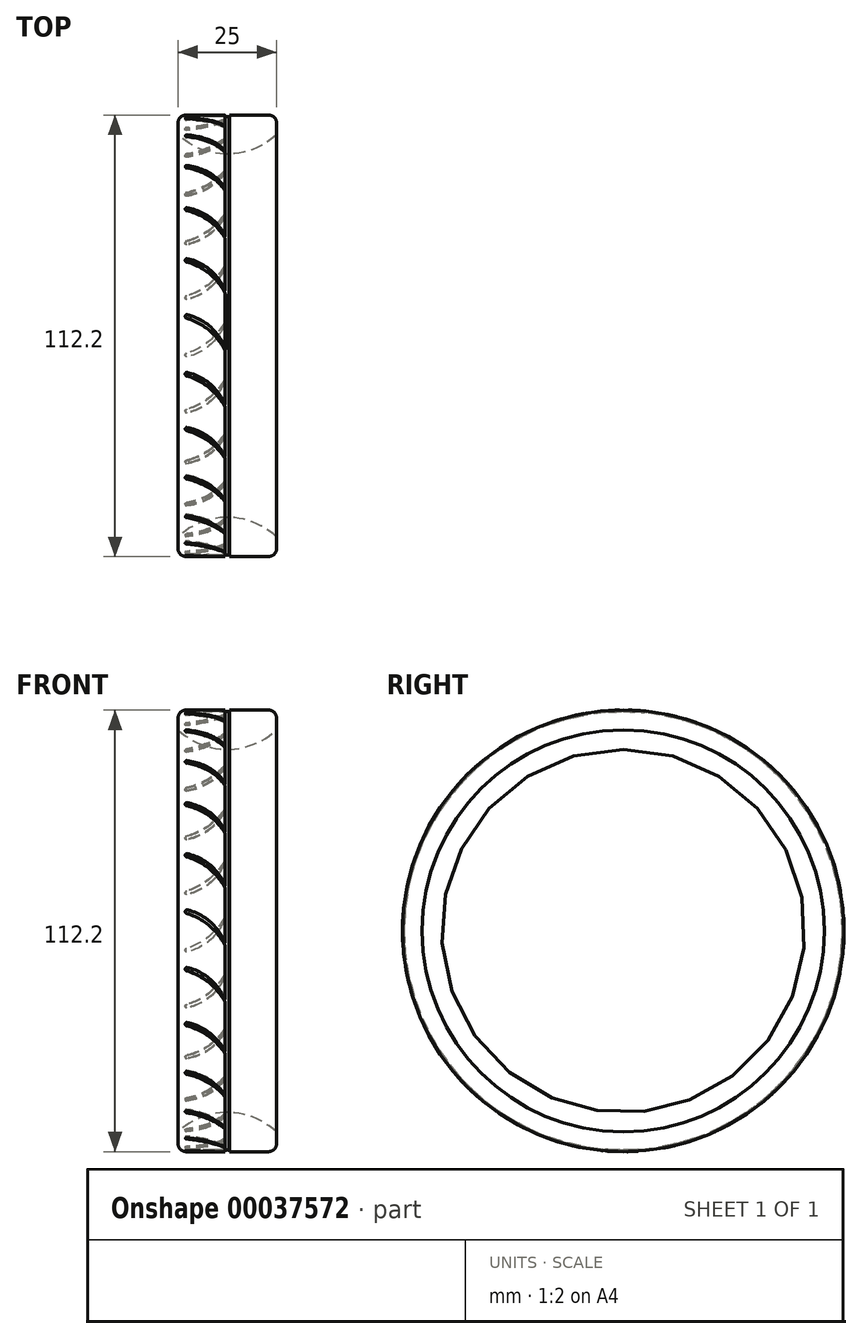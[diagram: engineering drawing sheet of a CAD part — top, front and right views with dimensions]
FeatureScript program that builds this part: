
annotation { "Feature Type Name" : "Feature", "Feature Type Description" : "" }
export const myFeature = defineFeature(function(context is Context, id is Id, definition is map)
    precondition{}
    {
        {
            var Q0;
            Q0=qCreatedBy(makeId("Top.planeOp"),FACE);
            var sketch = newSketch(context, id + "F0", { "sketchPlane" : qUnion([Q0])});
            skLineSegment(sketch, "E0", {"start": v(-134.1, 0) * mm, "end": v(143.87, 0) * mm, "construction": true});
            skLineSegment(sketch, "E1.left", {"start": v(-12.5, 54.1) * mm, "end": v(-12.5, 51.1) * mm});
            skLineSegment(sketch, "E1.right", {"start": v(12.5, 54.1) * mm, "end": v(12.5, 51.1) * mm});
            skArc(sketch, "E2", {"start": v(-12.5, 51.1) * mm, "mid": v(0, 46.14) * mm, "end": v(12.5, 51.1) * mm});
            skLineSegment(sketch, "E3", {"start": v(-10.5, 56.1) * mm, "end": v(-0.6, 56.1) * mm});
            skPoint(sketch, "E4.visualSharp", {"position": v(-12.5, 56.1) * mm});
            skArc(sketch, "E4.filletArc", {"start": v(-10.5, 56.1) * mm, "mid": v(-11.91, 55.51) * mm, "end": v(-12.5, 54.1) * mm});
            skPoint(sketch, "E5.visualSharp", {"position": v(12.5, 56.1) * mm});
            skArc(sketch, "E5.filletArc", {"start": v(12.5, 54.1) * mm, "mid": v(11.91, 55.51) * mm, "end": v(10.5, 56.1) * mm});
            skLineSegment(sketch, "E6.rect.bottom", {"start": v(0.6, 55.7) * mm, "end": v(-0.6, 55.7) * mm});
            skLineSegment(sketch, "E6.rect.left", {"start": v(0.6, 55.7) * mm, "end": v(0.6, 56.1) * mm});
            skLineSegment(sketch, "E6.rect.right", {"start": v(-0.6, 55.7) * mm, "end": v(-0.6, 56.1) * mm});
            skLineSegment(sketch, "E7.trimOffspring", {"start": v(0.6, 56.1) * mm, "end": v(10.5, 56.1) * mm});
            skSolve(sketch);
        }
        {
            var Q0;
            Q0=makeQuery(id+"F0.imprint","IMPRINT",FACE,{"disambiguationData":[TD([[makeQuery(id+"F0.imprint","IMPRINT",EDGE,{"derivedFrom":sQuery(id+"F0.wireOp",EDGE,"E1.left")}),1.0]])]});
            var Q1;
            Q1=sQuery(id+"F0.wireOp",EDGE,"E0");
            revolve(context, id + "F1", {"entities" : qUnion([Q0]), "axis" : qUnion([Q1]), "revolveType" : RevolveType.FULL});
        }
        {
            var Q0;
            Q0=qCreatedBy(makeId("Top.planeOp"),FACE);
            cPlane(context, id + "F2", {"entities" : qUnion([Q0]), "cplaneType" : CPlaneType.OFFSET, "offset" : 56.1 * mm, "width" : 150 * mm, "height" : 150 * mm});
        }
        {
            var Q0;
            Q0=qCreatedBy(makeId("Top.planeOp"),FACE);
            var sketch = newSketch(context, id + "F3", { "sketchPlane" : qUnion([Q0])});
            skLineSegment(sketch, "E8", {"start": v(-88.22, 0) * mm, "end": v(82.6, 0) * mm, "construction": true});
            skSolve(sketch);
        }
        {
            var Q0;
            Q0=qCreatedBy(id+"F2.planeOp",FACE);
            var sketch = newSketch(context, id + "F4", { "sketchPlane" : qUnion([Q0])});
            skArc(sketch, "E9", {"start": v(0, -5.08) * mm, "mid": v(-3.64, 1.64) * mm, "end": v(-10.3, 5.36) * mm});
            skArc(sketch, "E10", {"start": v(0, -5.08) * mm, "mid": v(-4.05, 0.87) * mm, "end": v(-10.3, 4.43) * mm});
            skArc(sketch, "E11", {"start": v(-10.3, 5.36) * mm, "mid": v(-10.68, 4.9) * mm, "end": v(-10.3, 4.43) * mm});
            skArc(sketch, "E12.MirrorCS", {"start": v(0, -5.08) * mm, "mid": v(3.64, 1.64) * mm, "end": v(10.3, 5.36) * mm});
            skArc(sketch, "E13.MirrorCS", {"start": v(0, -5.08) * mm, "mid": v(4.05, 0.87) * mm, "end": v(10.3, 4.43) * mm});
            skArc(sketch, "E14.MirrorCS", {"start": v(10.3, 5.36) * mm, "mid": v(10.68, 4.9) * mm, "end": v(10.3, 4.43) * mm});
            skSolve(sketch);
        }
        {
            var Q0;
            Q0=makeQuery(id+"F4.imprint","IMPRINT",FACE,{"disambiguationData":[TD([[makeQuery(id+"F4.imprint","IMPRINT",EDGE,{"derivedFrom":sQuery(id+"F4.wireOp",EDGE,"E9")}),1.0]])]});
            var Q1;
            Q1=makeQuery(id+"F4.imprint","IMPRINT",FACE,{"disambiguationData":[TD([[makeQuery(id+"F4.imprint","IMPRINT",EDGE,{"derivedFrom":sQuery(id+"F4.wireOp",EDGE,"E12.MirrorCS")}),-1.0]])]});
            var Q2;
            Q2=makeQuery(id+"F1.opRevolve","SWEPT_FACE",FACE,{"disambiguationData":[OSD([sQuery(id+"F0.wireOp",EDGE,"E6.rect.bottom")])]});
            extrude(context, id + "F5", {"entities" : qUnion([Q0, Q1]), "operationType" : NewBodyOperationType.REMOVE, "endBound" : BoundingType.UP_TO_SURFACE, "oppositeDirection" : true, "endBoundEntityFace" : qUnion([Q2]), "depth" : 1 * mm});
        }
        {
            var Q0;
            Q0=makeQuery(id+"F5.boolean.opBoolean","COPY",FACE,{"derivedFrom":makeQuery(id+"F5.opExtrude","SWEPT_FACE",FACE,{"disambiguationData":[OSD([sQuery(id+"F4.wireOp",EDGE,"E9")])]})});
            var Q1;
            Q1=makeQuery(id+"F5.boolean.opBoolean","COPY",FACE,{"derivedFrom":makeQuery(id+"F5.opExtrude","SWEPT_FACE",FACE,{"disambiguationData":[OSD([sQuery(id+"F4.wireOp",EDGE,"E11")])]})});
            var Q2;
            Q2=makeQuery(id+"F5.boolean.opBoolean","COPY",FACE,{"derivedFrom":makeQuery(id+"F5.opExtrude","SWEPT_FACE",FACE,{"disambiguationData":[OSD([sQuery(id+"F4.wireOp",EDGE,"E12.MirrorCS")])]})});
            var Q3;
            Q3=makeQuery(id+"F5.boolean.opBoolean","COPY",FACE,{"derivedFrom":makeQuery(id+"F5.opExtrude","SWEPT_FACE",FACE,{"disambiguationData":[OSD([sQuery(id+"F4.wireOp",EDGE,"E10")])]})});
            var Q4;
            Q4=makeQuery(id+"F5.boolean.opBoolean","COPY",FACE,{"derivedFrom":makeQuery(id+"F5.opExtrude","SWEPT_FACE",FACE,{"disambiguationData":[OSD([sQuery(id+"F4.wireOp",EDGE,"E13.MirrorCS")])]})});
            var Q5;
            Q5=makeQuery(id+"F5.boolean.opBoolean","COPY",FACE,{"derivedFrom":makeQuery(id+"F5.opExtrude","SWEPT_FACE",FACE,{"disambiguationData":[OSD([sQuery(id+"F4.wireOp",EDGE,"E14.MirrorCS")])]})});
            var Q6;
            Q6=sQuery(id+"F3.wireOp",EDGE,"E8");
            circularPattern(context, id + "F6", {"faces" : qUnion([Q0, Q1, Q2, Q3, Q4, Q5]), "axis" : qUnion([Q6]), "angle" : 360 * degree, "instanceCount" : 24, "equalSpace" : true, "patternType" : PatternType.FACE});
        }
        {
            var Q0;
            Q0=makeQuery(id+"F6.opPattern","SPLIT",EDGE,{"disambiguationData":[OD(0.0)],"derivedFrom":makeQuery(id+"F1.opRevolve","SWEPT_EDGE",EDGE,{"disambiguationData":[OSD([sQuery(id+"F0.wireOp",EDGE,"E6.rect.bottom"),sQuery(id+"F0.wireOp",EDGE,"E6.rect.left")])]})});
            var Q1;
            Q1=makeQuery(id+"F5.boolean.opBoolean","COPY",EDGE,{"derivedFrom":makeQuery(id+"F5.opExtrude","TWEAK_EDGE",EDGE,{"derivedFrom":[makeQuery(id+"F1.opRevolve","SWEPT_FACE",FACE,{"disambiguationData":[OSD([sQuery(id+"F0.wireOp",EDGE,"E6.rect.bottom")])]}),makeQuery(id+"F4.imprint","IMPRINT",EDGE,{"derivedFrom":sQuery(id+"F4.wireOp",EDGE,"E12.MirrorCS")})]})});
            var Q2;
            Q2=makeQuery(id+"F5.boolean.opBoolean","COPY",EDGE,{"derivedFrom":makeQuery(id+"F5.opExtrude","TWEAK_EDGE",EDGE,{"derivedFrom":[makeQuery(id+"F1.opRevolve","SWEPT_FACE",FACE,{"disambiguationData":[OSD([sQuery(id+"F0.wireOp",EDGE,"E6.rect.bottom")])]}),makeQuery(id+"F4.imprint","IMPRINT",EDGE,{"derivedFrom":sQuery(id+"F4.wireOp",EDGE,"E14.MirrorCS")})]})});
            var Q3;
            Q3=makeQuery(id+"F5.boolean.opBoolean","COPY",EDGE,{"derivedFrom":makeQuery(id+"F5.opExtrude","TWEAK_EDGE",EDGE,{"derivedFrom":[makeQuery(id+"F1.opRevolve","SWEPT_FACE",FACE,{"disambiguationData":[OSD([sQuery(id+"F0.wireOp",EDGE,"E6.rect.bottom")])]}),makeQuery(id+"F4.imprint","IMPRINT",EDGE,{"derivedFrom":sQuery(id+"F4.wireOp",EDGE,"E13.MirrorCS")})]})});
            var Q4;
            Q4=makeQuery(id+"F6.opPattern","SPLIT",EDGE,{"disambiguationData":[OD(1.0)],"derivedFrom":makeQuery(id+"F1.opRevolve","SWEPT_EDGE",EDGE,{"disambiguationData":[OSD([sQuery(id+"F0.wireOp",EDGE,"E6.rect.bottom"),sQuery(id+"F0.wireOp",EDGE,"E6.rect.left")])]})});
            var Q5;
            Q5=makeQuery(id+"F6.opPattern","SPLIT",EDGE,{"disambiguationData":[OD(0.0)],"derivedFrom":makeQuery(id+"F1.opRevolve","SWEPT_EDGE",EDGE,{"disambiguationData":[OSD([sQuery(id+"F0.wireOp",EDGE,"E6.rect.bottom"),sQuery(id+"F0.wireOp",EDGE,"E6.rect.right")])]})});
            var Q6;
            Q6=makeQuery(id+"F5.boolean.opBoolean","COPY",EDGE,{"derivedFrom":makeQuery(id+"F5.opExtrude","TWEAK_EDGE",EDGE,{"derivedFrom":[makeQuery(id+"F1.opRevolve","SWEPT_FACE",FACE,{"disambiguationData":[OSD([sQuery(id+"F0.wireOp",EDGE,"E6.rect.bottom")])]}),makeQuery(id+"F4.imprint","IMPRINT",EDGE,{"derivedFrom":sQuery(id+"F4.wireOp",EDGE,"E9")})]})});
            var Q7;
            Q7=makeQuery(id+"F5.boolean.opBoolean","COPY",EDGE,{"derivedFrom":makeQuery(id+"F5.opExtrude","TWEAK_EDGE",EDGE,{"derivedFrom":[makeQuery(id+"F1.opRevolve","SWEPT_FACE",FACE,{"disambiguationData":[OSD([sQuery(id+"F0.wireOp",EDGE,"E6.rect.bottom")])]}),makeQuery(id+"F4.imprint","IMPRINT",EDGE,{"derivedFrom":sQuery(id+"F4.wireOp",EDGE,"E10")})]})});
            var Q8;
            Q8=makeQuery(id+"F5.boolean.opBoolean","COPY",EDGE,{"derivedFrom":makeQuery(id+"F5.opExtrude","TWEAK_EDGE",EDGE,{"derivedFrom":[makeQuery(id+"F1.opRevolve","SWEPT_FACE",FACE,{"disambiguationData":[OSD([sQuery(id+"F0.wireOp",EDGE,"E6.rect.bottom")])]}),makeQuery(id+"F4.imprint","IMPRINT",EDGE,{"derivedFrom":sQuery(id+"F4.wireOp",EDGE,"E11")})]})});
            chamfer(context, id + "F7", {"entities" : qUnion([Q0, Q1, Q2, Q3, Q4, Q5, Q6, Q7, Q8]), "chamferType" : ChamferType.TWO_OFFSETS, "width1" : .15 * mm, "oppositeDirection" : false, "width2" : .2 * mm});
        }
    });
